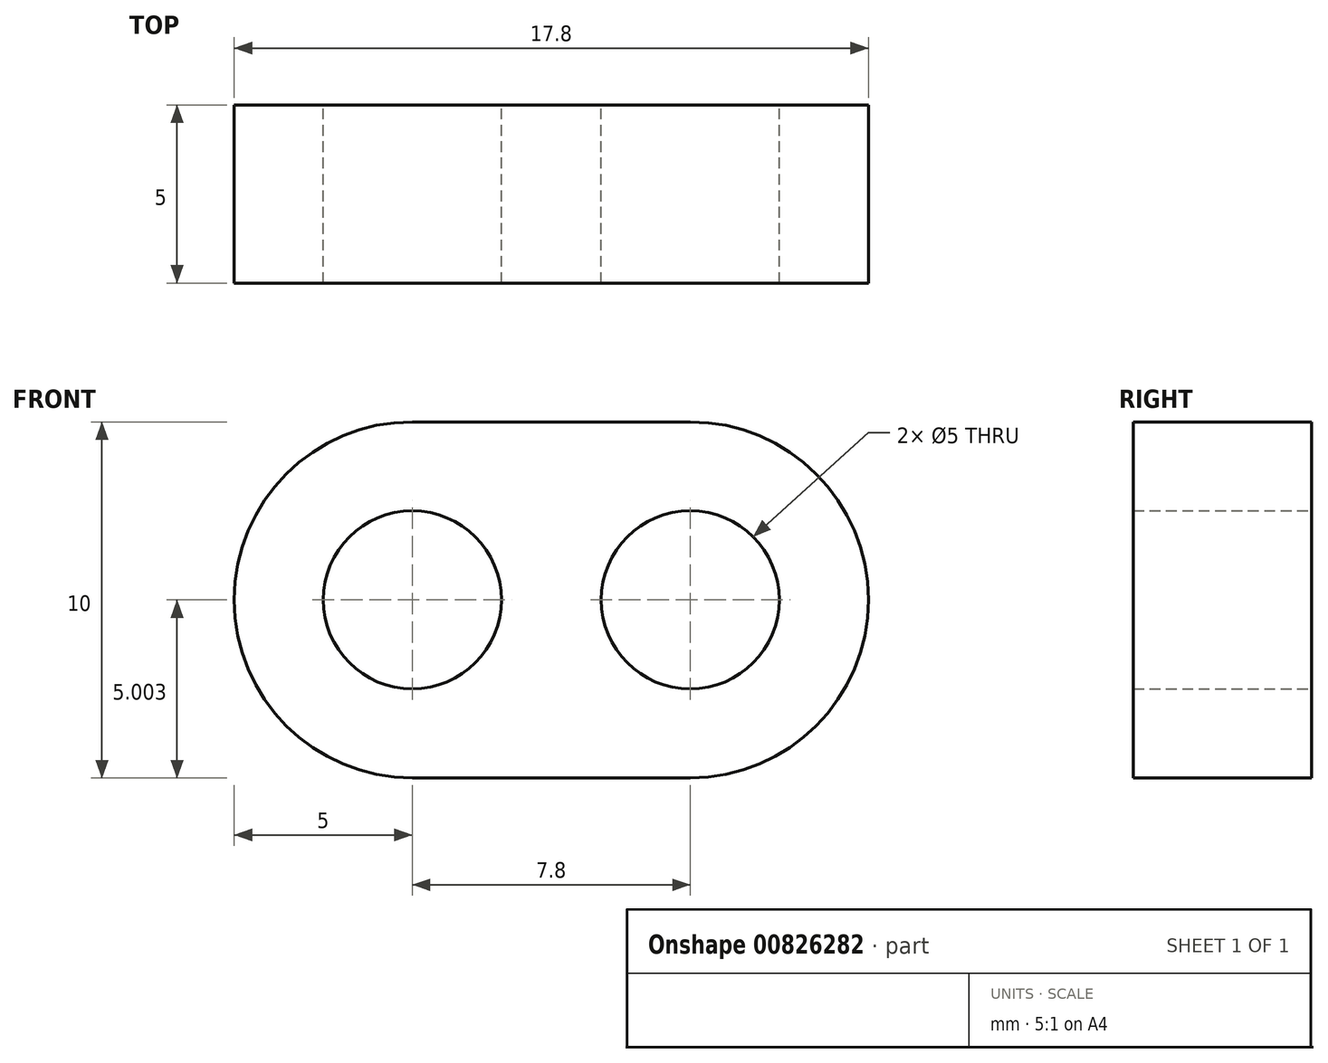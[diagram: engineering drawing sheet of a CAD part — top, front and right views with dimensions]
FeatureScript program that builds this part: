
annotation { "Feature Type Name" : "Feature", "Feature Type Description" : "" }
export const myFeature = defineFeature(function(context is Context, id is Id, definition is map)
    precondition{}
    {
        {
            var Q0;
            Q0=qCreatedBy(makeId("Front.planeOp"),FACE);
            var sketch = newSketch(context, id + "F0", { "sketchPlane" : qUnion([Q0])});
            skArc(sketch, "E0", {"start": v(0, 23.93) * mm, "mid": v(-5, 18.93) * mm, "end": v(0, 13.93) * mm});
            skArc(sketch, "E1", {"start": v(7.8, 13.93) * mm, "mid": v(12.8, 18.93) * mm, "end": v(7.8, 23.93) * mm});
            skLineSegment(sketch, "E2", {"start": v(0, 23.93) * mm, "end": v(7.8, 23.93) * mm});
            skLineSegment(sketch, "E3", {"start": v(0, 13.93) * mm, "end": v(7.8, 13.93) * mm});
            skCircle(sketch, "E4", {"center": v(0, 18.93) * mm, "radius": 2.5 * mm});
            skCircle(sketch, "E5", {"center": v(7.8, 18.93) * mm, "radius": 2.5 * mm});
            skSolve(sketch);
        }
        {
            var Q0;
            Q0 = qSketchRegion(id + "F0", true);
            extrude(context, id + "F1", {"entities" : qUnion([Q0]), "depth" : 5 * mm, "offsetDistance" : 25 * mm});
        }
    });
